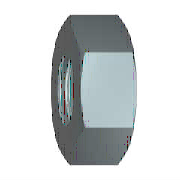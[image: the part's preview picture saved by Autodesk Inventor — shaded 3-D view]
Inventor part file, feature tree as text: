
AUTODESK INVENTOR PART (.ipt)
format: ipt  version: 2020 (Build 240168000, 168)  size: 163,840 bytes
history: native  units: mm (DEFAULTED — no unit token found)
features: sketch x3, other x2, extrude x1, hole x1, plane x1
ambient origin geometry x7: Origin, YZ Plane, XZ Plane, X Axis, Y Axis, Z Axis, Center Point
bodies: Solid1 (feature_tree)
feature tree (8):
  extrude  "Bryła"  Depth=5.773503mm
  other  "Faza1"
  hole  "Gwint"  [1 undecoded]
  other  "Work Axis1"
  plane  "Work Plane1"
  sketch  "Szkic1"
  sketch  "Szkic2"
  sketch  "Szkic3"
note: 1 required parameter value undecoded (feature->parameter linkage not recoverable at this tier; creation-order binding heuristic only, values carry confidence <= 0.55)
